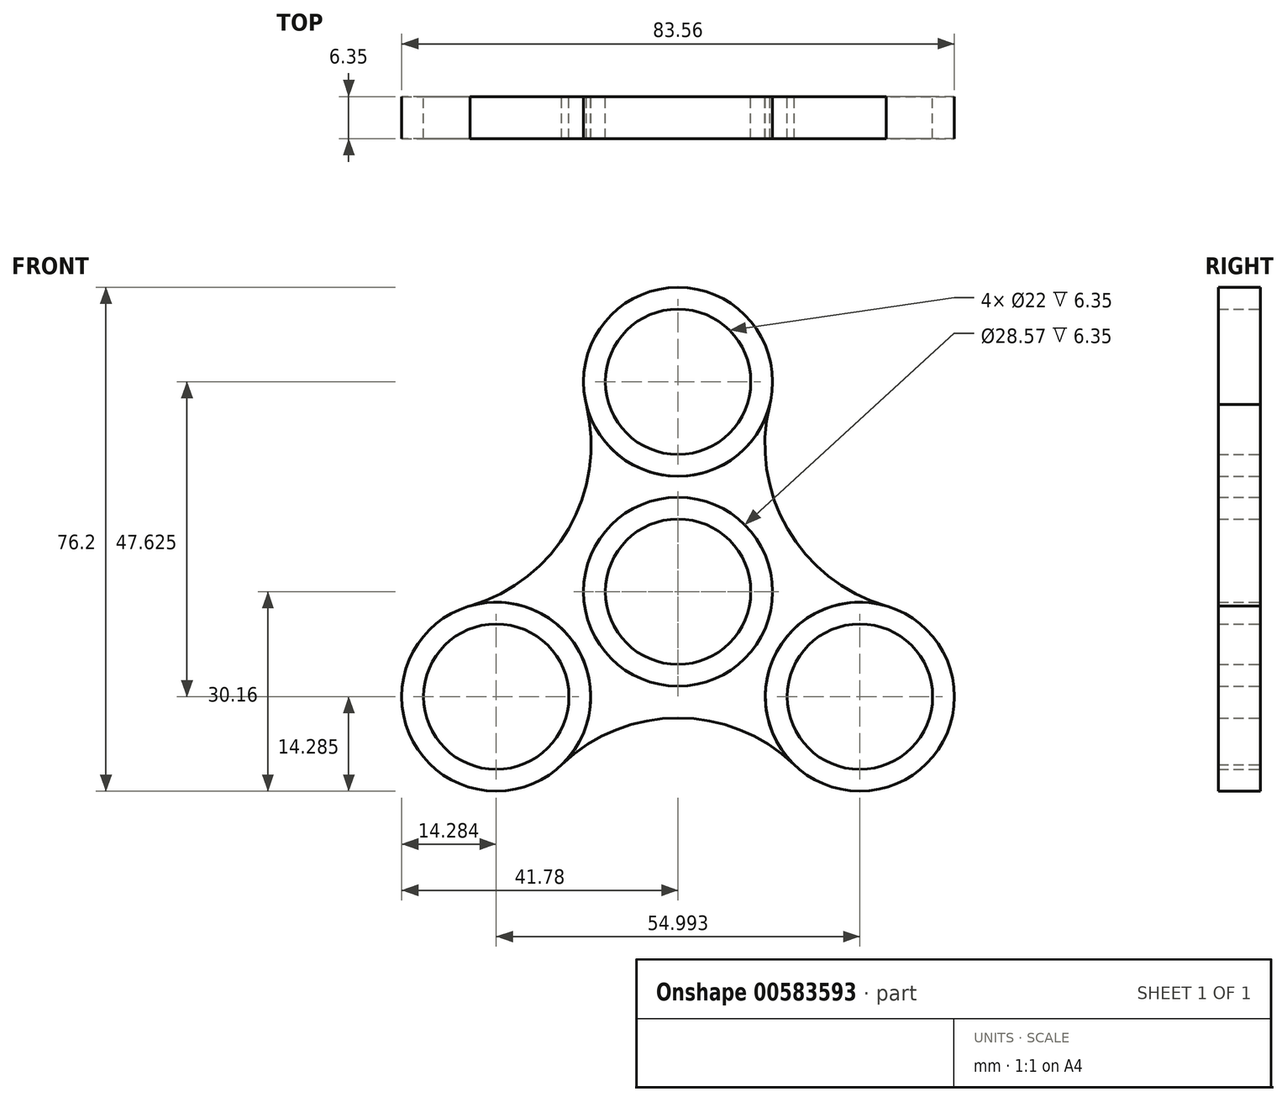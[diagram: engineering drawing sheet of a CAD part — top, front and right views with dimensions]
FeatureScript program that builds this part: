
annotation { "Feature Type Name" : "Feature", "Feature Type Description" : "" }
export const myFeature = defineFeature(function(context is Context, id is Id, definition is map)
    precondition{}
    {
        {
            var Q0;
            Q0=qCreatedBy(makeId("Front.planeOp"),FACE);
            var sketch = newSketch(context, id + "F0", { "sketchPlane" : qUnion([Q0])});
            skCircle(sketch, "E0", {"center": v(0, 0) * mm, "radius": 11 * mm});
            skCircle(sketch, "E1", {"center": v(0, 0) * mm, "radius": 14.29 * mm});
            skCircle(sketch, "E2", {"center": v(0, 31.75) * mm, "radius": 11 * mm});
            skCircle(sketch, "E3", {"center": v(0, 31.75) * mm, "radius": 14.29 * mm});
            skCircle(sketch, "E4.1.0", {"center": v(-27.5, -15.87) * mm, "radius": 14.29 * mm});
            skCircle(sketch, "E5", {"center": v(27.5, -15.88) * mm, "radius": 14.29 * mm});
            skCircle(sketch, "E6", {"center": v(-27.5, -15.87) * mm, "radius": 11 * mm});
            skCircle(sketch, "E7", {"center": v(27.5, -15.88) * mm, "radius": 11 * mm});
            skSolve(sketch);
        }
        {
            var Q0;
            Q0=qCreatedBy(makeId("Front.planeOp"),FACE);
            var sketch = newSketch(context, id + "F1", { "sketchPlane" : qUnion([Q0])});
            skArc(sketch, "E8", {"start": v(-31.47, -2.15) * mm, "mid": v(-16.54, 9.55) * mm, "end": v(-13.87, 28.33) * mm});
            skArc(sketch, "E9", {"start": v(13.87, 28.33) * mm, "mid": v(16.54, 9.55) * mm, "end": v(31.47, -2.15) * mm});
            skArc(sketch, "E10", {"start": v(17.6, -26.18) * mm, "mid": v(0, -19.1) * mm, "end": v(-17.6, -26.18) * mm});
            skCircle(sketch, "E11.0", {"center": v(0, 31.75) * mm, "radius": 14.29 * mm});
            skCircle(sketch, "E12.0", {"center": v(0, 0) * mm, "radius": 14.29 * mm});
            skCircle(sketch, "E13.0", {"center": v(27.5, -15.88) * mm, "radius": 14.29 * mm});
            skCircle(sketch, "E14.0", {"center": v(-27.5, -15.87) * mm, "radius": 14.29 * mm});
            skSolve(sketch);
        }
        {
            var Q0;
            Q0=makeQuery(id+"F0.imprint","IMPRINT",FACE,{"disambiguationData":[TD([[makeQuery(id+"F0.imprint","IMPRINT",EDGE,{"derivedFrom":sQuery(id+"F0.wireOp",EDGE,"E4.1.0")}),1.0]])]});
            var Q1;
            {var subQ1=sQuery(id+"F1.wireOp",EDGE,"E8");Q1=makeQuery(id+"F1.imprint","IMPRINT",FACE,{"disambiguationData":[TD([[makeQuery(id+"F1.imprint","IMPRINT",EDGE,{"derivedFrom":subQ1}),-1.0]])]});}
            var Q2;
            Q2=makeQuery(id+"F0.imprint","IMPRINT",FACE,{"disambiguationData":[TD([[makeQuery(id+"F0.imprint","IMPRINT",EDGE,{"derivedFrom":sQuery(id+"F0.wireOp",EDGE,"E0")}),-1.0]])]});
            var Q3;
            Q3=makeQuery(id+"F0.imprint","IMPRINT",FACE,{"disambiguationData":[TD([[makeQuery(id+"F0.imprint","IMPRINT",EDGE,{"derivedFrom":sQuery(id+"F0.wireOp",EDGE,"E2")}),-1.0]])]});
            var Q4;
            Q4=makeQuery(id+"F0.imprint","IMPRINT",FACE,{"disambiguationData":[TD([[makeQuery(id+"F0.imprint","IMPRINT",EDGE,{"derivedFrom":sQuery(id+"F0.wireOp",EDGE,"E5")}),1.0]])]});
            extrude(context, id + "F2", {"entities" : qUnion([Q0, Q1, Q2, Q3, Q4]), "depth" : 6.35 * mm, "offsetDistance" : 25.4 * mm});
        }
    });
